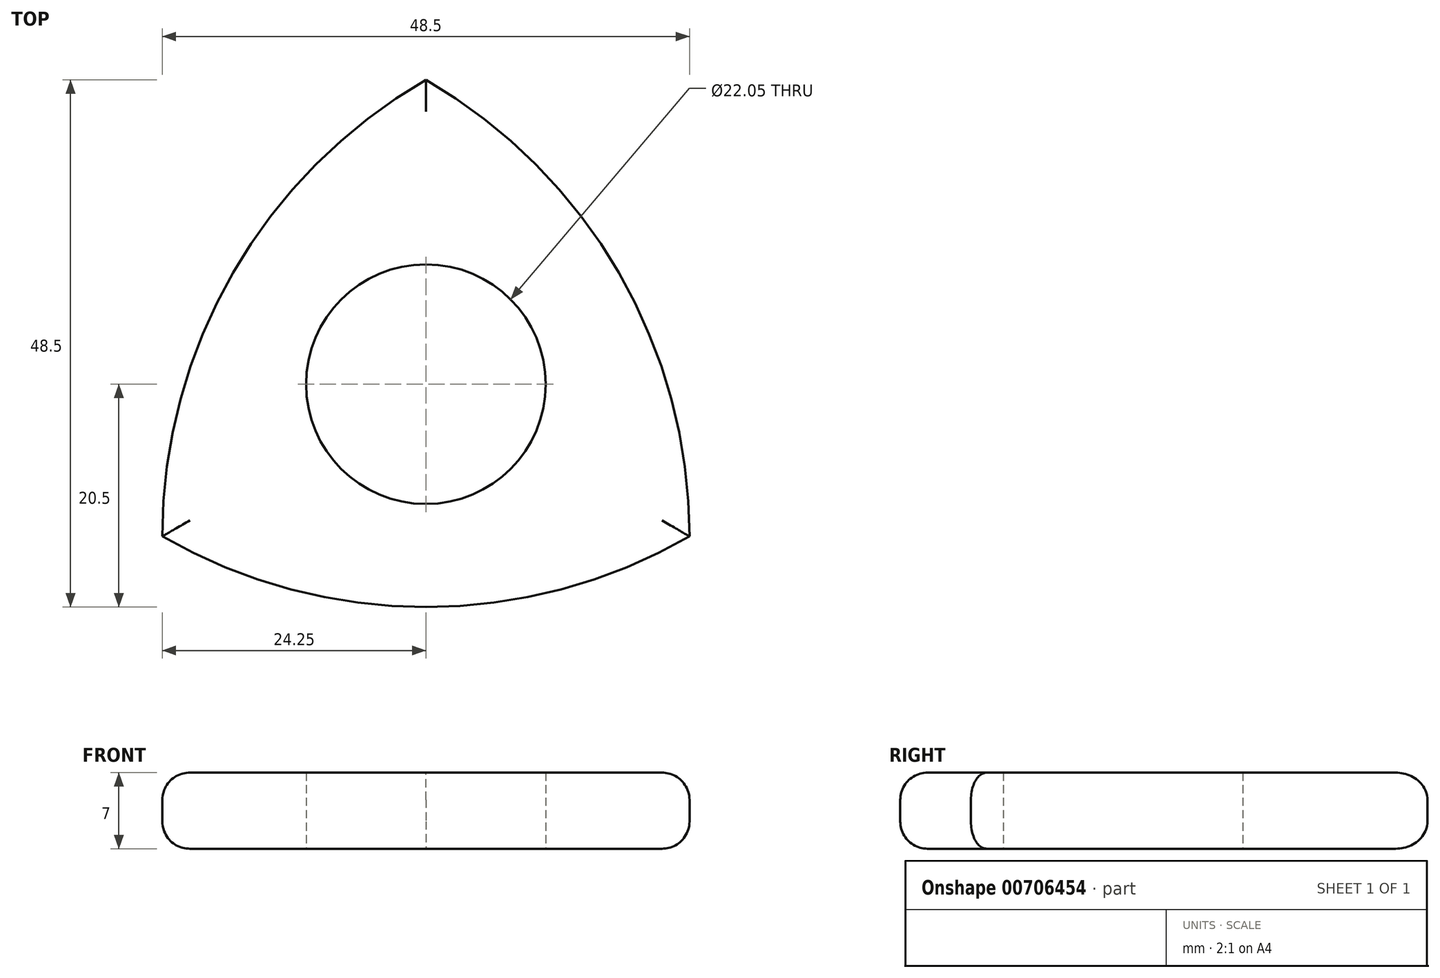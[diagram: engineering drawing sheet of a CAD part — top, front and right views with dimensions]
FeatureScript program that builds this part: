
annotation { "Feature Type Name" : "Feature", "Feature Type Description" : "" }
export const myFeature = defineFeature(function(context is Context, id is Id, definition is map)
    precondition{}
    {
        {
            var Q0;
            Q0=qCreatedBy(makeId("Top.planeOp"),FACE);
            var sketch = newSketch(context, id + "F0", { "sketchPlane" : qUnion([Q0])});
            skCircle(sketch, "E0.cCircle", {"center": v(0, 0) * mm, "radius": 14 * mm, "construction": true});
            skLineSegment(sketch, "E0.0", {"start": v(24.25, -14) * mm, "end": v(-24.25, -14) * mm});
            skLineSegment(sketch, "E0.1", {"start": v(-24.25, -14) * mm, "end": v(0, 28) * mm});
            skLineSegment(sketch, "E0.2", {"start": v(0, 28) * mm, "end": v(24.25, -14) * mm});
            skPoint(sketch, "E0.0.midPoint", {"position": v(0, -14) * mm});
            skCircle(sketch, "E1", {"center": v(0, 0) * mm, "radius": 11.03 * mm});
            skArc(sketch, "E2", {"start": v(-24.25, -14) * mm, "mid": v(0, -20.5) * mm, "end": v(24.25, -14) * mm});
            skArc(sketch, "E3", {"start": v(0, 28) * mm, "mid": v(-17.75, 10.25) * mm, "end": v(-24.25, -14) * mm});
            skArc(sketch, "E4", {"start": v(24.25, -14) * mm, "mid": v(17.75, 10.25) * mm, "end": v(0, 28) * mm});
            skSolve(sketch);
        }
        {
            var Q0;
            Q0=makeQuery(id+"F0.imprint","IMPRINT",FACE,{"disambiguationData":[TD([[makeQuery(id+"F0.imprint","IMPRINT",EDGE,{"derivedFrom":sQuery(id+"F0.wireOp",EDGE,"E0.1")}),1.0]])]});
            var Q1;
            Q1=makeQuery(id+"F0.imprint","IMPRINT",FACE,{"disambiguationData":[TD([[makeQuery(id+"F0.imprint","IMPRINT",EDGE,{"derivedFrom":sQuery(id+"F0.wireOp",EDGE,"E0.0")}),-1.0]])]});
            var Q2;
            Q2=makeQuery(id+"F0.imprint","IMPRINT",FACE,{"disambiguationData":[TD([[makeQuery(id+"F0.imprint","IMPRINT",EDGE,{"derivedFrom":sQuery(id+"F0.wireOp",EDGE,"E0.2")}),1.0]])]});
            var Q3;
            Q3=makeQuery(id+"F0.imprint","IMPRINT",FACE,{"disambiguationData":[TD([[makeQuery(id+"F0.imprint","IMPRINT",EDGE,{"derivedFrom":sQuery(id+"F0.wireOp",EDGE,"E0.0")}),1.0]])]});
            extrude(context, id + "F1", {"entities" : qUnion([Q0, Q1, Q2, Q3]), "depth" : 7 * mm, "offsetDistance" : 25 * mm});
        }
        {
            var Q0;
            Q0=makeQuery(id+"F1.opExtrude","CAP_EDGE",EDGE,{"disambiguationData":[OSD([sQuery(id+"F0.wireOp",EDGE,"E2")])],"isStart":false});
            var Q1;
            Q1=makeQuery(id+"F1.opExtrude","CAP_EDGE",EDGE,{"disambiguationData":[OSD([sQuery(id+"F0.wireOp",EDGE,"E4")])],"isStart":false});
            var Q2;
            Q2=makeQuery(id+"F1.opExtrude","CAP_EDGE",EDGE,{"disambiguationData":[OSD([sQuery(id+"F0.wireOp",EDGE,"E3")])],"isStart":false});
            var Q3;
            Q3=makeQuery(id+"F1.opExtrude","CAP_EDGE",EDGE,{"disambiguationData":[OSD([sQuery(id+"F0.wireOp",EDGE,"E2")])],"isStart":true});
            var Q4;
            Q4=makeQuery(id+"F1.opExtrude","CAP_EDGE",EDGE,{"disambiguationData":[OSD([sQuery(id+"F0.wireOp",EDGE,"E4")])],"isStart":true});
            var Q5;
            Q5=makeQuery(id+"F1.opExtrude","CAP_EDGE",EDGE,{"disambiguationData":[OSD([sQuery(id+"F0.wireOp",EDGE,"E3")])],"isStart":true});
            fillet(context, id + "F2", {"entities" : qUnion([Q0, Q1, Q2, Q3, Q4, Q5]), "radius" : 2.5 * mm, "tangentPropagation" : true, "allowEdgeOverflow" : false});
        }
    });
